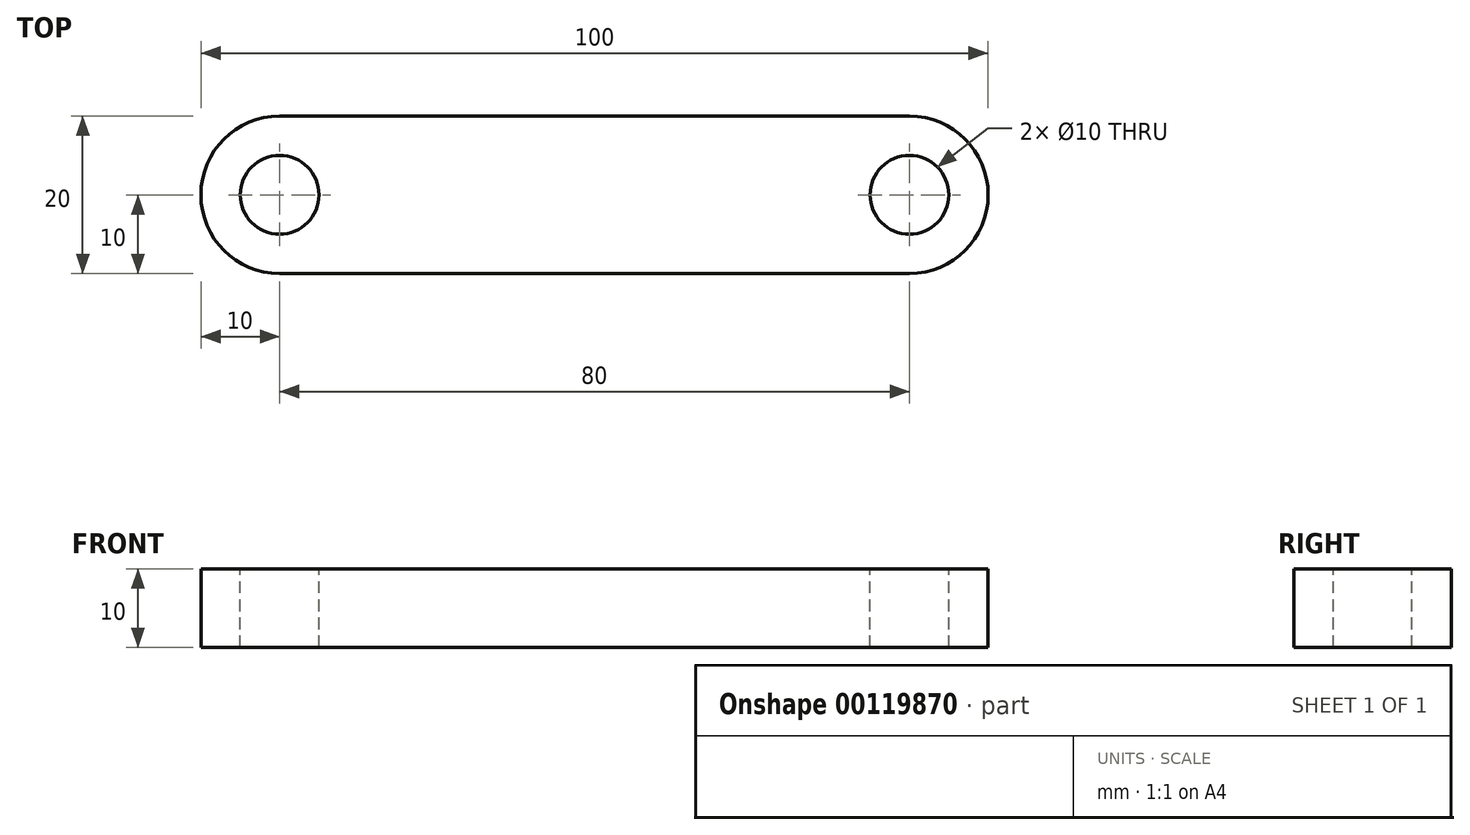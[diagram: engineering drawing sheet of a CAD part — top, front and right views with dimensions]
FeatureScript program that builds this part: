
annotation { "Feature Type Name" : "Feature", "Feature Type Description" : "" }
export const myFeature = defineFeature(function(context is Context, id is Id, definition is map)
    precondition{}
    {
        {
            var Q0;
            Q0=qCreatedBy(makeId("Top.planeOp"),FACE);
            var sketch = newSketch(context, id + "F0", { "sketchPlane" : qUnion([Q0])});
            skLineSegment(sketch, "E0", {"start": v(0, 0) * mm, "end": v(0, 20) * mm, "construction": true});
            skLineSegment(sketch, "E1", {"start": v(0, 20) * mm, "end": v(80, 20) * mm, "construction": true});
            skLineSegment(sketch, "E2", {"start": v(80, 20) * mm, "end": v(80, 0) * mm, "construction": true});
            skArc(sketch, "E3", {"start": v(0, 20) * mm, "mid": v(-10, 10) * mm, "end": v(0, 0) * mm});
            skArc(sketch, "E4", {"start": v(80, 0) * mm, "mid": v(90, 10) * mm, "end": v(80, 20) * mm});
            skLineSegment(sketch, "E5", {"start": v(0, 0) * mm, "end": v(80, 0) * mm});
            skLineSegment(sketch, "E6", {"start": v(80, 20) * mm, "end": v(0, 20) * mm});
            skSolve(sketch);
        }
        {
            var Q0;
            Q0=makeQuery(id+"F0.imprint","IMPRINT",FACE,{"disambiguationData":[TD([[makeQuery(id+"F0.imprint","IMPRINT",EDGE,{"derivedFrom":sQuery(id+"F0.wireOp",EDGE,"E3")}),1.0]])]});
            extrude(context, id + "F1", {"entities" : qUnion([Q0]), "depth" : 10 * mm});
        }
        {
            var Q0;
            Q0=makeQuery(id+"F1.opExtrude","CAP_FACE",FACE,{"disambiguationData":[OSD([sQuery(id+"F0.wireOp",EDGE,"E3"),sQuery(id+"F0.wireOp",EDGE,"E4"),sQuery(id+"F0.wireOp",EDGE,"E5"),sQuery(id+"F0.wireOp",EDGE,"E6")])],"isStart":false});
            var sketch = newSketch(context, id + "F2", { "sketchPlane" : qUnion([Q0])});
            skLineSegment(sketch, "E7", {"start": v(0, 0) * mm, "end": v(0, 10) * mm, "construction": true});
            skLineSegment(sketch, "E8", {"start": v(0, 10) * mm, "end": v(80, 10) * mm, "construction": true});
            skCircle(sketch, "E9", {"center": v(0, 10) * mm, "radius": 5 * mm});
            skCircle(sketch, "E10", {"center": v(80, 10) * mm, "radius": 5 * mm});
            skSolve(sketch);
        }
        {
            var Q0;
            Q0 = qSketchRegion(id + "F2", true);
            var Q1;
            Q1=sQuery(id+"F2.wireOp",EDGE,"E9");
            var Q2;
            Q2=sQuery(id+"F2.wireOp",EDGE,"E10");
            extrude(context, id + "F3", {"entities" : qUnion([Q0]), "operationType" : NewBodyOperationType.REMOVE, "surfaceEntities" : qUnion([Q1, Q2]), "oppositeDirection" : true, "depth" : 10 * mm});
        }
    });
